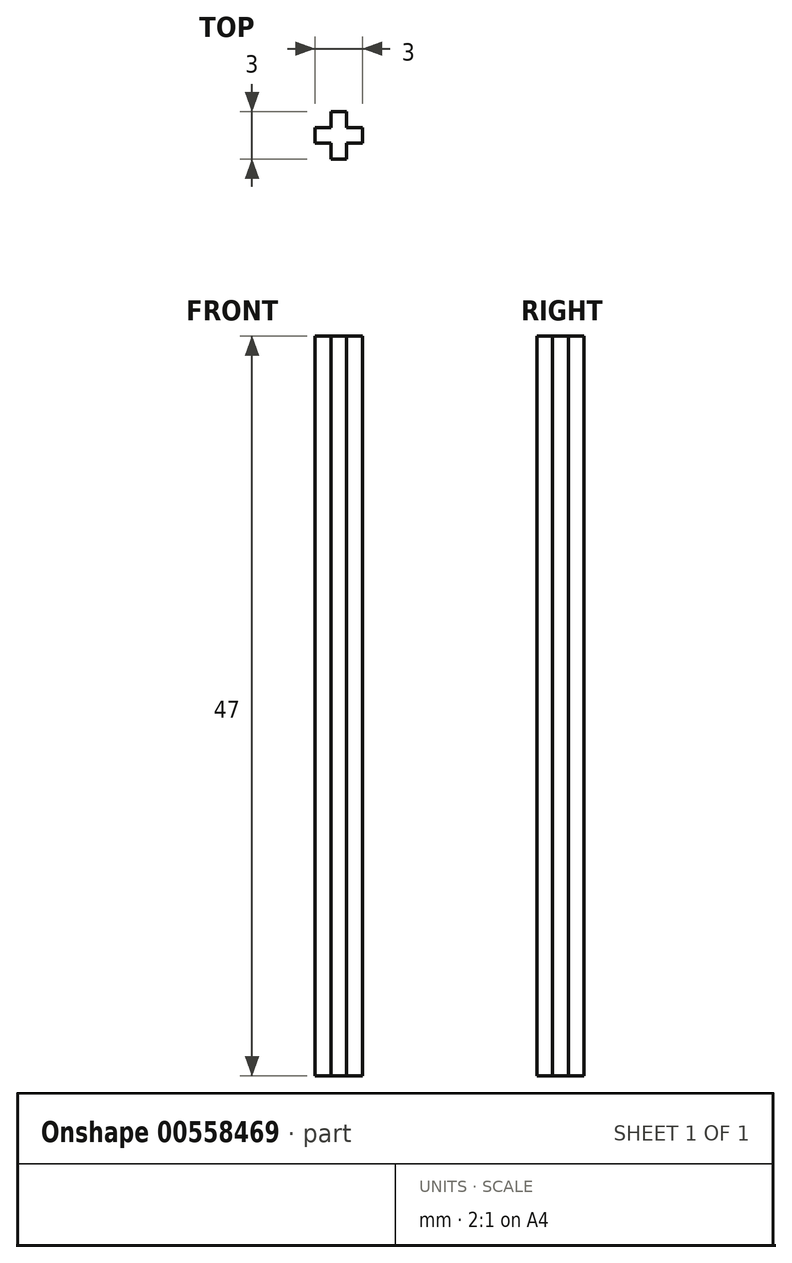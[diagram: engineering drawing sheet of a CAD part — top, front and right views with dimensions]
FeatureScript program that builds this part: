
annotation { "Feature Type Name" : "Feature", "Feature Type Description" : "" }
export const myFeature = defineFeature(function(context is Context, id is Id, definition is map)
    precondition{}
    {
        {
            var Q0;
            Q0=qCreatedBy(makeId("Top.planeOp"),FACE);
            var sketch = newSketch(context, id + "F0", { "sketchPlane" : qUnion([Q0])});
            skLineSegment(sketch, "E0", {"start": v(0, 0) * mm, "end": v(0, -1) * mm});
            skLineSegment(sketch, "E1", {"start": v(0, -1) * mm, "end": v(1, -1) * mm});
            skLineSegment(sketch, "E2", {"start": v(1, -1) * mm, "end": v(1, 0) * mm});
            skLineSegment(sketch, "E3", {"start": v(1, 0) * mm, "end": v(2, 0) * mm});
            skLineSegment(sketch, "E4", {"start": v(2, 0) * mm, "end": v(2, 1) * mm});
            skLineSegment(sketch, "E5", {"start": v(2, 1) * mm, "end": v(1, 1) * mm});
            skLineSegment(sketch, "E6", {"start": v(1, 1) * mm, "end": v(1, 2) * mm});
            skLineSegment(sketch, "E7", {"start": v(1, 2) * mm, "end": v(0, 2) * mm});
            skLineSegment(sketch, "E8", {"start": v(0, 2) * mm, "end": v(0, 1) * mm});
            skLineSegment(sketch, "E9", {"start": v(0, 1) * mm, "end": v(-1, 1) * mm});
            skLineSegment(sketch, "E10", {"start": v(-1, 1) * mm, "end": v(-1, 0) * mm});
            skLineSegment(sketch, "E11", {"start": v(-1, 0) * mm, "end": v(0, 0) * mm});
            skSolve(sketch);
        }
        {
            var Q0;
            Q0=makeQuery(id+"F0.imprint","IMPRINT",FACE,{"disambiguationData":[TD([[makeQuery(id+"F0.imprint","IMPRINT",EDGE,{"derivedFrom":sQuery(id+"F0.wireOp",EDGE,"E0")}),1.0]])]});
            extrude(context, id + "F1", {"entities" : qUnion([Q0]), "depth" : 47 * mm, "offsetDistance" : 25.4 * mm});
        }
    });
